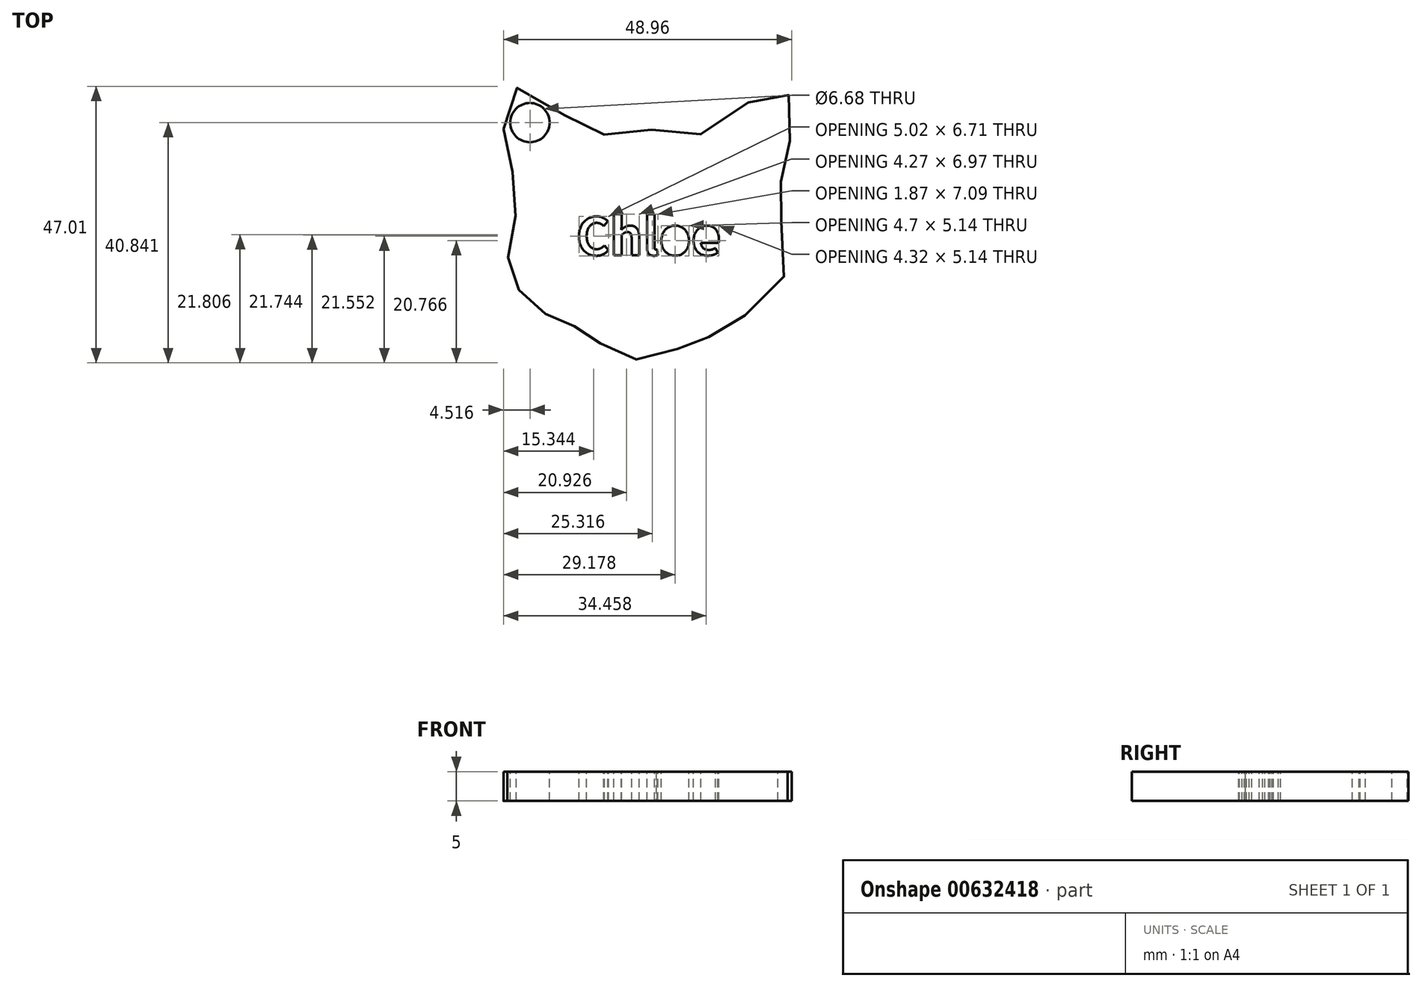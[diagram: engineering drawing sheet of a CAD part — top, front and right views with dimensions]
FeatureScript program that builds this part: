
annotation { "Feature Type Name" : "Feature", "Feature Type Description" : "" }
export const myFeature = defineFeature(function(context is Context, id is Id, definition is map)
    precondition{}
    {
        {
            var Q0;
            Q0=qCreatedBy(makeId("Top.planeOp"),FACE);
            var sketch = newSketch(context, id + "F0", { "sketchPlane" : qUnion([Q0])});
            skFitSpline(sketch, "E0", {"points": [v(-14.2, 49.76) * mm, v(-14.86, 47.12) * mm, v(-15.5, 43.62) * mm, v(-15.88, 42.16) * mm, v(-16.2, 39.8) * mm, v(-15.72, 36.45) * mm, v(-14.64, 31.6) * mm, v(-15.34, 26.31) * mm, v(-18.3, 22.27) * mm, v(-23.1, 19.58) * mm, v(-26.5, 18.01) * mm, v(-27.63, 16.72) * mm, v(-29.36, 15.7) * mm, v(-31.4, 15.16) * mm, v(-32.65, 14.83) * mm, v(-35.66, 12.62) * mm, v(-38.58, 12.08) * mm, v(-41.32, 13.16) * mm, v(-43.05, 14.46) * mm, v(-45.95, 15.24) * mm, v(-48.06, 15.96) * mm, v(-48.94, 16.63) * mm, v(-50.15, 17.84) * mm, v(-51.94, 18.87) * mm, v(-53.48, 19.53) * mm, v(-54.68, 19.92) * mm, v(-56.28, 20.66) * mm, v(-57.95, 21.95) * mm, v(-59.65, 23.65) * mm, v(-60.6, 25.04) * mm, v(-61.51, 26.91) * mm, v(-61.89, 28.6) * mm, v(-62.16, 31.45) * mm, v(-61.55, 33.97) * mm, v(-60.74, 37.33) * mm, v(-60.74, 40.66) * mm, v(-61.12, 43.8) * mm, v(-62.08, 47.65) * mm, v(-62.72, 51.5) * mm, v(-62.79, 51.56) * mm, v(-62.68, 56.16) * mm, v(-61.57, 58.78) * mm, v(-57.34, 57.44) * mm, v(-53.3, 54.75) * mm, v(-50.23, 52.44) * mm, v(-47.54, 50.9) * mm, v(-43.7, 51.1) * mm, v(-40.44, 51.3) * mm, v(-36.02, 51.68) * mm, v(-31.8, 50.71) * mm, v(-28.33, 51.3) * mm, v(-23.72, 54.56) * mm, v(-18.92, 57.82) * mm, v(-15.85, 58.97) * mm, v(-14, 56.77) * mm, v(-14, 54.75) * mm, v(-14.2, 49.76) * mm]});
            skText(sketch, "E1", { "text": "Chloe", "fontName": "NotoSansCJKtc-Bold.otf"});
            skCircle(sketch, "E2", {"center": v(-58.34, 52.87) * mm, "radius": 3.34 * mm});
            const initialGuessF0  = {"E1": [-0.0505, 0.03035, 1, 0, 0.00629]};
            skSetInitialGuess(sketch, initialGuessF0);
            skSolve(sketch);
        }
        {
            var Q0;
            Q0=makeQuery(id+"F0.imprint","IMPRINT",FACE,{"disambiguationData":[TD([[makeQuery(id+"F0.imprint","IMPRINT",EDGE,{"derivedFrom":sQuery(id+"F0.wireOp",EDGE,"E0")}),-1.0]])]});
            extrude(context, id + "F1", {"entities" : qUnion([Q0]), "oppositeDirection" : true, "depth" : 5 * mm, "offsetDistance" : 25 * mm});
        }
    });
